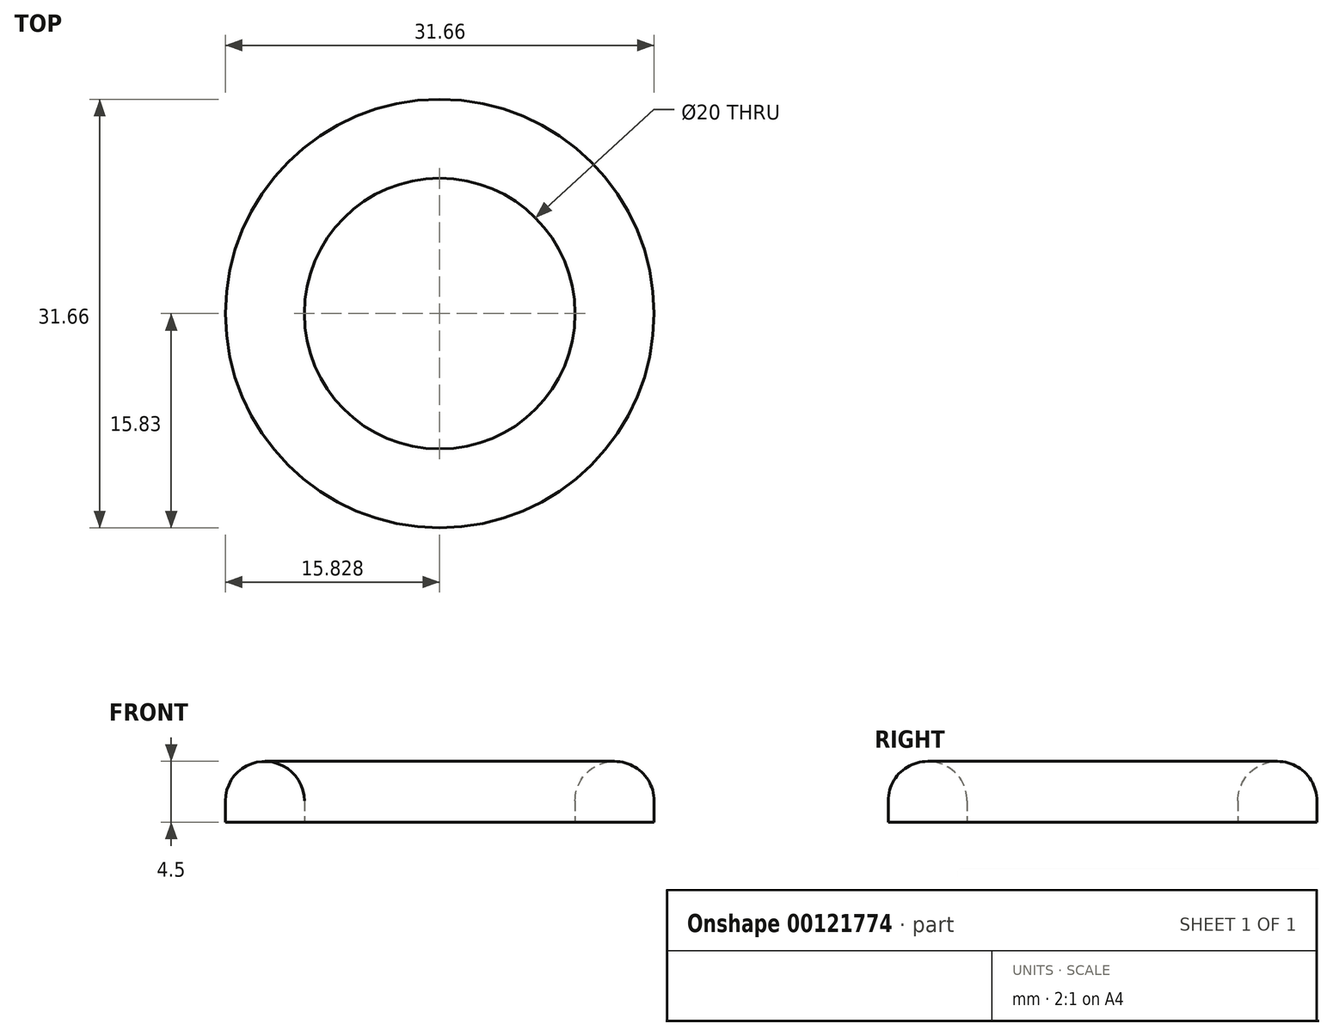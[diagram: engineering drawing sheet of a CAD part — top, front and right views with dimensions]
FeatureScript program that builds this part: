
annotation { "Feature Type Name" : "Feature", "Feature Type Description" : "" }
export const myFeature = defineFeature(function(context is Context, id is Id, definition is map)
    precondition{}
    {
        {
            var Q0;
            Q0=qCreatedBy(makeId("Front.planeOp"),FACE);
            var sketch = newSketch(context, id + "F0", { "sketchPlane" : qUnion([Q0])});
            skLineSegment(sketch, "E0.bottom", {"start": v(0, 0) * mm, "end": v(5.83, 0) * mm});
            skLineSegment(sketch, "E0.left", {"start": v(0, 0) * mm, "end": v(0, 1.58) * mm});
            skLineSegment(sketch, "E0.right", {"start": v(5.83, 0) * mm, "end": v(5.83, 1.58) * mm});
            skArc(sketch, "E1", {"start": v(5.83, 1.58) * mm, "mid": v(2.91, 4.5) * mm, "end": v(0, 1.58) * mm});
            skLineSegment(sketch, "E2", {"start": v(15.83, 0) * mm, "end": v(15.83, 7.57) * mm});
            skSolve(sketch);
        }
        {
            var Q0;
            Q0=makeQuery(id+"F0.imprint","IMPRINT",FACE,{"disambiguationData":[TD([[makeQuery(id+"F0.imprint","IMPRINT",EDGE,{"derivedFrom":sQuery(id+"F0.wireOp",EDGE,"E0.bottom")}),1.0]])]});
            var Q1;
            Q1=sQuery(id+"F0.wireOp",EDGE,"E2");
            revolve(context, id + "F1", {"entities" : qUnion([Q0]), "axis" : qUnion([Q1]), "revolveType" : RevolveType.FULL});
        }
    });
